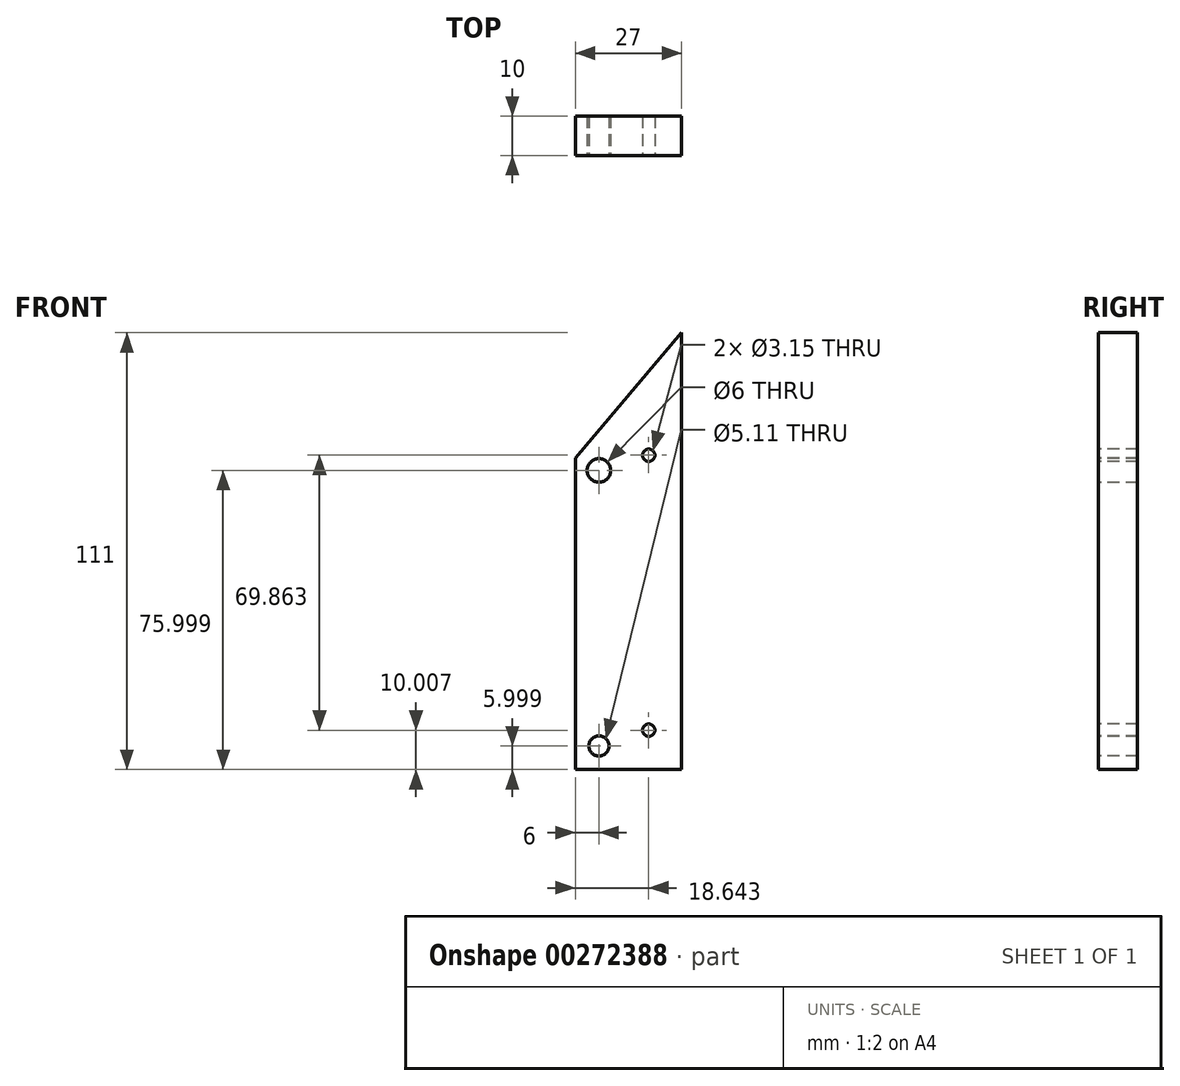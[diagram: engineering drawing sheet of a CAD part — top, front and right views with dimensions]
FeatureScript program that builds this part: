
annotation { "Feature Type Name" : "Feature", "Feature Type Description" : "" }
export const myFeature = defineFeature(function(context is Context, id is Id, definition is map)
    precondition{}
    {
        {
            var Q0;
            Q0=qCreatedBy(makeId("Front.planeOp"),FACE);
            var sketch = newSketch(context, id + "F0", { "sketchPlane" : qUnion([Q0])});
            skLineSegment(sketch, "E0", {"start": v(-57.89, 1.52) * mm, "end": v(-30.89, 1.52) * mm});
            skLineSegment(sketch, "E1", {"start": v(-30.89, 1.52) * mm, "end": v(-30.89, 112.52) * mm});
            skLineSegment(sketch, "E2", {"start": v(-30.89, 112.52) * mm, "end": v(-57.89, 80.63) * mm});
            skLineSegment(sketch, "E3", {"start": v(-57.89, 80.63) * mm, "end": v(-57.89, 1.52) * mm});
            skCircle(sketch, "E4", {"center": v(-51.89, 77.52) * mm, "radius": 3 * mm});
            skPoint(sketch, "E4.first.point", {"position": v(-54.89, 77.52) * mm});
            skPoint(sketch, "E4.second.point", {"position": v(-51.89, 80.52) * mm});
            skPoint(sketch, "E4.third.point", {"position": v(-49.98, 75.2) * mm});
            skCircle(sketch, "E5", {"center": v(-51.89, 7.52) * mm, "radius": 2.55 * mm});
            skPoint(sketch, "E5.first.point", {"position": v(-54.44, 7.52) * mm});
            skPoint(sketch, "E5.second.point", {"position": v(-51.89, 10.07) * mm});
            skPoint(sketch, "E5.third.point", {"position": v(-49.98, 5.82) * mm});
            skCircle(sketch, "E6", {"center": v(-39.25, 11.53) * mm, "radius": 1.57 * mm});
            skPoint(sketch, "E6.first.point", {"position": v(-39.48, 13.08) * mm});
            skPoint(sketch, "E6.second.point", {"position": v(-37.67, 11.53) * mm});
            skPoint(sketch, "E6.third.point", {"position": v(-40.32, 10.38) * mm});
            skCircle(sketch, "E7", {"center": v(-39.25, 81.39) * mm, "radius": 1.57 * mm});
            skPoint(sketch, "E7.first.point", {"position": v(-40.69, 82.03) * mm});
            skPoint(sketch, "E7.second.point", {"position": v(-38.06, 82.42) * mm});
            skPoint(sketch, "E7.third.point", {"position": v(-38.79, 79.88) * mm});
            skLineSegment(sketch, "E8", {"start": v(-51.89, 7.52) * mm, "end": v(-57.89, 7.52) * mm, "construction": true});
            skLineSegment(sketch, "E9", {"start": v(-51.89, 7.52) * mm, "end": v(-51.89, 1.52) * mm, "construction": true});
            skLineSegment(sketch, "E10", {"start": v(-51.89, 7.52) * mm, "end": v(-51.89, 77.52) * mm, "construction": true});
            skSolve(sketch);
        }
        {
            var Q0;
            Q0=makeQuery(id+"F0.imprint","IMPRINT",FACE,{"disambiguationData":[TD([[makeQuery(id+"F0.imprint","IMPRINT",EDGE,{"derivedFrom":sQuery(id+"F0.wireOp",EDGE,"E0")}),1.0]])]});
            extrude(context, id + "F1", {"entities" : qUnion([Q0]), "oppositeDirection" : true, "depth" : 10 * mm});
        }
    });
